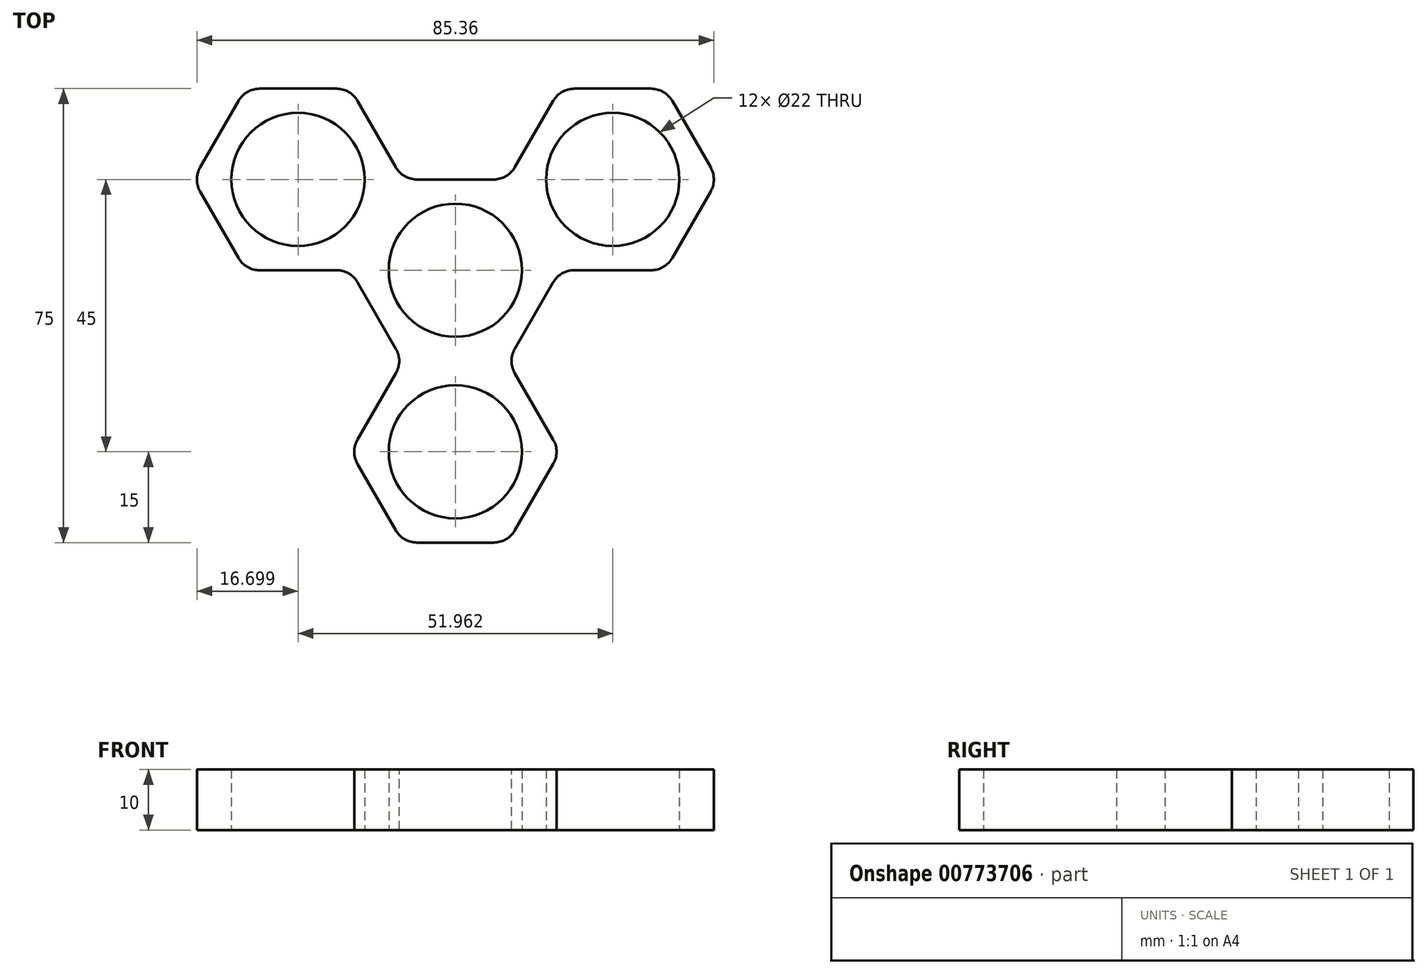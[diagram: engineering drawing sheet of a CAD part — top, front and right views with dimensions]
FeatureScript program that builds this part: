
annotation { "Feature Type Name" : "Feature", "Feature Type Description" : "" }
export const myFeature = defineFeature(function(context is Context, id is Id, definition is map)
    precondition{}
    {
        {
            var Q0;
            Q0=qCreatedBy(makeId("Top.planeOp"),FACE);
            var sketch = newSketch(context, id + "F0", { "sketchPlane" : qUnion([Q0])});
            skCircle(sketch, "E0.cCircle", {"center": v(0, 0) * mm, "radius": 15 * mm, "construction": true});
            skLineSegment(sketch, "E0.0", {"start": v(8.66, -15) * mm, "end": v(-8.66, -15) * mm});
            skLineSegment(sketch, "E0.1", {"start": v(-8.66, -15) * mm, "end": v(-17.32, 0) * mm});
            skLineSegment(sketch, "E0.2", {"start": v(-17.32, 0) * mm, "end": v(-8.66, 15) * mm});
            skLineSegment(sketch, "E0.3", {"start": v(-8.66, 15) * mm, "end": v(8.66, 15) * mm});
            skLineSegment(sketch, "E0.4", {"start": v(8.66, 15) * mm, "end": v(17.32, 0) * mm});
            skLineSegment(sketch, "E0.5", {"start": v(17.32, 0) * mm, "end": v(8.66, -15) * mm});
            skPoint(sketch, "E0.0.midPoint", {"position": v(0, -15) * mm});
            skCircle(sketch, "E1.cCircle", {"center": v(25.98, 15) * mm, "radius": 15 * mm, "construction": true});
            skLineSegment(sketch, "E1.0", {"start": v(34.64, 0) * mm, "end": v(17.32, 0) * mm});
            skLineSegment(sketch, "E1.1", {"start": v(17.32, 0) * mm, "end": v(8.66, 15) * mm});
            skLineSegment(sketch, "E1.2", {"start": v(8.66, 15) * mm, "end": v(17.32, 30) * mm});
            skLineSegment(sketch, "E1.3", {"start": v(17.32, 30) * mm, "end": v(34.64, 30) * mm});
            skLineSegment(sketch, "E1.4", {"start": v(34.64, 30) * mm, "end": v(43.3, 15) * mm});
            skLineSegment(sketch, "E1.5", {"start": v(43.3, 15) * mm, "end": v(34.64, 0) * mm});
            skPoint(sketch, "E1.0.midPoint", {"position": v(25.98, 0) * mm});
            skCircle(sketch, "E2.cCircle", {"center": v(-25.98, 15) * mm, "radius": 15 * mm, "construction": true});
            skLineSegment(sketch, "E2.0", {"start": v(-17.32, 0) * mm, "end": v(-34.64, 0) * mm});
            skLineSegment(sketch, "E2.1", {"start": v(-34.64, 0) * mm, "end": v(-43.3, 15) * mm});
            skLineSegment(sketch, "E2.2", {"start": v(-43.3, 15) * mm, "end": v(-34.64, 30) * mm});
            skLineSegment(sketch, "E2.3", {"start": v(-34.64, 30) * mm, "end": v(-17.32, 30) * mm});
            skLineSegment(sketch, "E2.4", {"start": v(-17.32, 30) * mm, "end": v(-8.66, 15) * mm});
            skLineSegment(sketch, "E2.5", {"start": v(-8.66, 15) * mm, "end": v(-17.32, 0) * mm});
            skPoint(sketch, "E2.0.midPoint", {"position": v(-25.98, 0) * mm});
            skCircle(sketch, "E3.cCircle", {"center": v(0, -30) * mm, "radius": 15 * mm, "construction": true});
            skLineSegment(sketch, "E3.0", {"start": v(8.66, -45) * mm, "end": v(-8.66, -45) * mm});
            skLineSegment(sketch, "E3.1", {"start": v(-8.66, -45) * mm, "end": v(-17.32, -30) * mm});
            skLineSegment(sketch, "E3.2", {"start": v(-17.32, -30) * mm, "end": v(-8.66, -15) * mm});
            skLineSegment(sketch, "E3.3", {"start": v(-8.66, -15) * mm, "end": v(8.66, -15) * mm});
            skLineSegment(sketch, "E3.4", {"start": v(8.66, -15) * mm, "end": v(17.32, -30) * mm});
            skLineSegment(sketch, "E3.5", {"start": v(17.32, -30) * mm, "end": v(8.66, -45) * mm});
            skPoint(sketch, "E3.0.midPoint", {"position": v(0, -45) * mm});
            skCircle(sketch, "E4", {"center": v(25.98, 15) * mm, "radius": 11 * mm});
            skCircle(sketch, "E5", {"center": v(0, 0) * mm, "radius": 11 * mm});
            skCircle(sketch, "E6", {"center": v(-25.98, 15) * mm, "radius": 11 * mm});
            skCircle(sketch, "E7", {"center": v(0, -30) * mm, "radius": 11 * mm});
            skSolve(sketch);
        }
        {
            var Q0;
            Q0=makeQuery(id+"F0.imprint","IMPRINT",FACE,{"disambiguationData":[TD([[makeQuery(id+"F0.imprint","IMPRINT",EDGE,{"derivedFrom":sQuery(id+"F0.wireOp",EDGE,"E2.0")}),-1.0]])]});
            var Q1;
            Q1=makeQuery(id+"F0.imprint","IMPRINT",FACE,{"disambiguationData":[TD([[makeQuery(id+"F0.imprint","IMPRINT",EDGE,{"derivedFrom":sQuery(id+"F0.wireOp",EDGE,"E0.1")}),-1.0]])]});
            var Q2;
            Q2=makeQuery(id+"F0.imprint","IMPRINT",FACE,{"disambiguationData":[TD([[makeQuery(id+"F0.imprint","IMPRINT",EDGE,{"derivedFrom":sQuery(id+"F0.wireOp",EDGE,"E1.0")}),-1.0]])]});
            var Q3;
            Q3=makeQuery(id+"F0.imprint","IMPRINT",FACE,{"disambiguationData":[TD([[makeQuery(id+"F0.imprint","IMPRINT",EDGE,{"derivedFrom":sQuery(id+"F0.wireOp",EDGE,"E3.0")}),-1.0]])]});
            extrude(context, id + "F1", {"entities" : qUnion([Q0, Q1, Q2, Q3]), "depth" : 10 * mm, "offsetDistance" : 25 * mm});
        }
        {
            var Q0;
            Q0=makeQuery(id+"F1.opExtrude","SWEPT_EDGE",EDGE,{"disambiguationData":[OSD([sQuery(id+"F0.wireOp",EDGE,"E3.0"),sQuery(id+"F0.wireOp",EDGE,"E3.5")])]});
            var Q1;
            Q1=makeQuery(id+"F1.opExtrude","SWEPT_EDGE",EDGE,{"disambiguationData":[OSD([sQuery(id+"F0.wireOp",EDGE,"E3.4"),sQuery(id+"F0.wireOp",EDGE,"E3.5")])]});
            var Q2;
            Q2=makeQuery(id+"F1.opExtrude","SWEPT_EDGE",EDGE,{"disambiguationData":[OSD([sQuery(id+"F0.wireOp",EDGE,"E0.5"),sQuery(id+"F0.wireOp",EDGE,"E3.3"),sQuery(id+"F0.wireOp",EDGE,"E3.4")])]});
            var Q3;
            Q3=makeQuery(id+"F1.opExtrude","SWEPT_EDGE",EDGE,{"disambiguationData":[OSD([sQuery(id+"F0.wireOp",EDGE,"E1.0"),sQuery(id+"F0.wireOp",EDGE,"E1.5")])]});
            var Q4;
            Q4=makeQuery(id+"F1.opExtrude","SWEPT_EDGE",EDGE,{"disambiguationData":[OSD([sQuery(id+"F0.wireOp",EDGE,"E0.5"),sQuery(id+"F0.wireOp",EDGE,"E1.0"),sQuery(id+"F0.wireOp",EDGE,"E1.1")])]});
            var Q5;
            Q5=makeQuery(id+"F1.opExtrude","SWEPT_EDGE",EDGE,{"disambiguationData":[OSD([sQuery(id+"F0.wireOp",EDGE,"E1.4"),sQuery(id+"F0.wireOp",EDGE,"E1.5")])]});
            var Q6;
            Q6=makeQuery(id+"F1.opExtrude","SWEPT_EDGE",EDGE,{"disambiguationData":[OSD([sQuery(id+"F0.wireOp",EDGE,"E1.3"),sQuery(id+"F0.wireOp",EDGE,"E1.4")])]});
            var Q7;
            Q7=makeQuery(id+"F1.opExtrude","SWEPT_EDGE",EDGE,{"disambiguationData":[OSD([sQuery(id+"F0.wireOp",EDGE,"E1.2"),sQuery(id+"F0.wireOp",EDGE,"E1.3")])]});
            var Q8;
            Q8=makeQuery(id+"F1.opExtrude","SWEPT_EDGE",EDGE,{"disambiguationData":[OSD([sQuery(id+"F0.wireOp",EDGE,"E0.3"),sQuery(id+"F0.wireOp",EDGE,"E1.1"),sQuery(id+"F0.wireOp",EDGE,"E1.2")])]});
            var Q9;
            Q9=makeQuery(id+"F1.opExtrude","SWEPT_EDGE",EDGE,{"disambiguationData":[OSD([sQuery(id+"F0.wireOp",EDGE,"E0.3"),sQuery(id+"F0.wireOp",EDGE,"E2.4"),sQuery(id+"F0.wireOp",EDGE,"E2.5")])]});
            var Q10;
            Q10=makeQuery(id+"F1.opExtrude","SWEPT_EDGE",EDGE,{"disambiguationData":[OSD([sQuery(id+"F0.wireOp",EDGE,"E2.3"),sQuery(id+"F0.wireOp",EDGE,"E2.4")])]});
            var Q11;
            Q11=makeQuery(id+"F1.opExtrude","SWEPT_EDGE",EDGE,{"disambiguationData":[OSD([sQuery(id+"F0.wireOp",EDGE,"E2.2"),sQuery(id+"F0.wireOp",EDGE,"E2.3")])]});
            var Q12;
            Q12=makeQuery(id+"F1.opExtrude","SWEPT_EDGE",EDGE,{"disambiguationData":[OSD([sQuery(id+"F0.wireOp",EDGE,"E2.1"),sQuery(id+"F0.wireOp",EDGE,"E2.2")])]});
            var Q13;
            Q13=makeQuery(id+"F1.opExtrude","SWEPT_EDGE",EDGE,{"disambiguationData":[OSD([sQuery(id+"F0.wireOp",EDGE,"E2.0"),sQuery(id+"F0.wireOp",EDGE,"E2.1")])]});
            var Q14;
            Q14=makeQuery(id+"F1.opExtrude","SWEPT_EDGE",EDGE,{"disambiguationData":[OSD([sQuery(id+"F0.wireOp",EDGE,"E0.1"),sQuery(id+"F0.wireOp",EDGE,"E2.0"),sQuery(id+"F0.wireOp",EDGE,"E2.5")])]});
            var Q15;
            Q15=makeQuery(id+"F1.opExtrude","SWEPT_EDGE",EDGE,{"disambiguationData":[OSD([sQuery(id+"F0.wireOp",EDGE,"E0.1"),sQuery(id+"F0.wireOp",EDGE,"E3.2"),sQuery(id+"F0.wireOp",EDGE,"E3.3")])]});
            var Q16;
            Q16=makeQuery(id+"F1.opExtrude","SWEPT_EDGE",EDGE,{"disambiguationData":[OSD([sQuery(id+"F0.wireOp",EDGE,"E3.1"),sQuery(id+"F0.wireOp",EDGE,"E3.2")])]});
            var Q17;
            Q17=makeQuery(id+"F1.opExtrude","SWEPT_EDGE",EDGE,{"disambiguationData":[OSD([sQuery(id+"F0.wireOp",EDGE,"E3.0"),sQuery(id+"F0.wireOp",EDGE,"E3.1")])]});
            fillet(context, id + "F2", {"entities" : qUnion([Q0, Q1, Q2, Q3, Q4, Q5, Q6, Q7, Q8, Q9, Q10, Q11, Q12, Q13, Q14, Q15, Q16, Q17]), "radius" : 4 * mm, "tangentPropagation" : true, "allowEdgeOverflow" : false});
        }
    });
